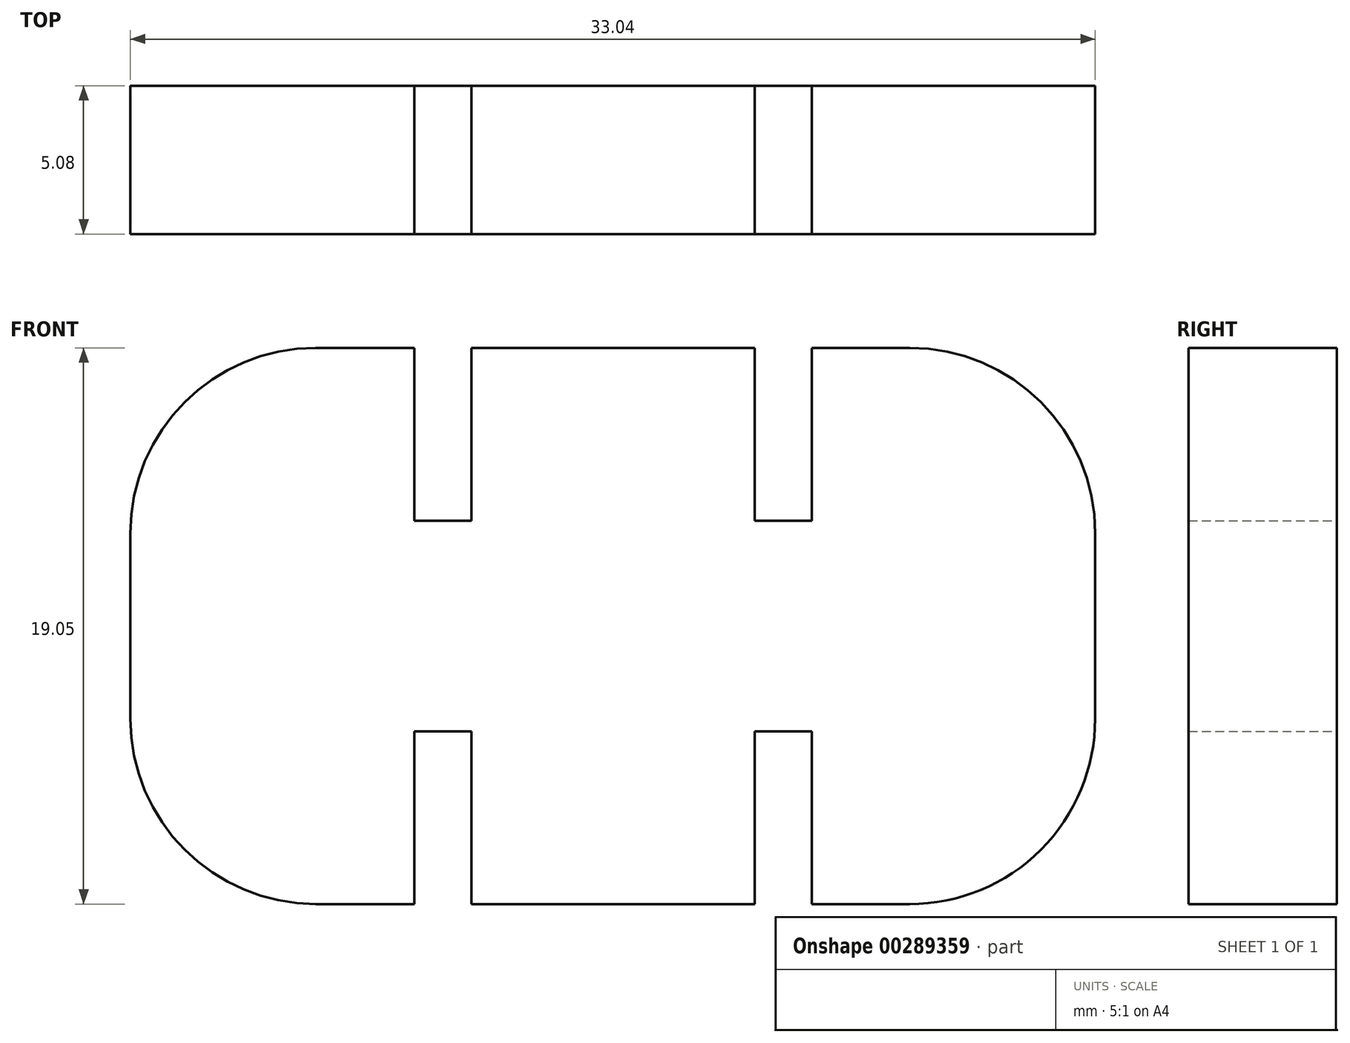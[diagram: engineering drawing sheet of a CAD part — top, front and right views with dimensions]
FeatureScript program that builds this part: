
annotation { "Feature Type Name" : "Feature", "Feature Type Description" : "" }
export const myFeature = defineFeature(function(context is Context, id is Id, definition is map)
    precondition{}
    {
        {
            var Q0;
            Q0=qCreatedBy(makeId("Front.planeOp"),FACE);
            var sketch = newSketch(context, id + "F0", { "sketchPlane" : qUnion([Q0])});
            skLineSegment(sketch, "E0", {"start": v(-67.37, 34.52) * mm, "end": v(-67.37, 28.17) * mm});
            skLineSegment(sketch, "E1", {"start": v(-61.02, 40.87) * mm, "end": v(-57.65, 40.87) * mm});
            skLineSegment(sketch, "E2", {"start": v(-57.65, 40.87) * mm, "end": v(-57.65, 34.95) * mm});
            skLineSegment(sketch, "E3", {"start": v(-57.65, 34.95) * mm, "end": v(-55.7, 34.95) * mm});
            skLineSegment(sketch, "E4", {"start": v(-55.7, 34.95) * mm, "end": v(-55.7, 40.87) * mm});
            skLineSegment(sketch, "E5", {"start": v(-55.7, 40.87) * mm, "end": v(-45.99, 40.87) * mm});
            skLineSegment(sketch, "E6", {"start": v(-45.99, 40.87) * mm, "end": v(-45.99, 34.95) * mm});
            skLineSegment(sketch, "E7", {"start": v(-45.99, 34.95) * mm, "end": v(-44.03, 34.95) * mm});
            skLineSegment(sketch, "E8", {"start": v(-44.03, 34.95) * mm, "end": v(-44.03, 40.87) * mm});
            skLineSegment(sketch, "E9", {"start": v(-44.03, 40.87) * mm, "end": v(-40.68, 40.87) * mm});
            skLineSegment(sketch, "E10", {"start": v(-34.33, 34.52) * mm, "end": v(-34.33, 28.17) * mm});
            skLineSegment(sketch, "E11", {"start": v(-61.02, 21.82) * mm, "end": v(-57.65, 21.82) * mm});
            skLineSegment(sketch, "E12", {"start": v(-57.65, 21.82) * mm, "end": v(-57.65, 27.74) * mm});
            skLineSegment(sketch, "E13", {"start": v(-57.65, 27.74) * mm, "end": v(-55.7, 27.74) * mm});
            skLineSegment(sketch, "E14", {"start": v(-55.7, 27.74) * mm, "end": v(-55.7, 21.82) * mm});
            skLineSegment(sketch, "E15", {"start": v(-55.7, 21.82) * mm, "end": v(-45.99, 21.82) * mm});
            skLineSegment(sketch, "E16", {"start": v(-45.99, 21.82) * mm, "end": v(-45.99, 27.74) * mm});
            skLineSegment(sketch, "E17", {"start": v(-45.99, 27.74) * mm, "end": v(-44.03, 27.74) * mm});
            skLineSegment(sketch, "E18", {"start": v(-44.03, 27.74) * mm, "end": v(-44.03, 21.82) * mm});
            skLineSegment(sketch, "E19", {"start": v(-44.03, 21.82) * mm, "end": v(-40.68, 21.82) * mm});
            skPoint(sketch, "E20.visualSharp", {"position": v(-67.37, 40.87) * mm});
            skArc(sketch, "E20.filletArc", {"start": v(-61.02, 40.87) * mm, "mid": v(-65.51, 39.01) * mm, "end": v(-67.37, 34.52) * mm});
            skPoint(sketch, "E21.visualSharp", {"position": v(-34.33, 40.87) * mm});
            skArc(sketch, "E21.filletArc", {"start": v(-34.33, 34.52) * mm, "mid": v(-36.19, 39) * mm, "end": v(-40.68, 40.87) * mm});
            skPoint(sketch, "E22.visualSharp", {"position": v(-34.33, 21.82) * mm});
            skArc(sketch, "E22.filletArc", {"start": v(-40.68, 21.82) * mm, "mid": v(-36.19, 23.68) * mm, "end": v(-34.33, 28.17) * mm});
            skPoint(sketch, "E23.visualSharp", {"position": v(-67.37, 21.82) * mm});
            skArc(sketch, "E23.filletArc", {"start": v(-67.37, 28.17) * mm, "mid": v(-65.51, 23.68) * mm, "end": v(-61.02, 21.82) * mm});
            skSolve(sketch);
        }
        {
            var Q0;
            Q0=makeQuery(id+"F0.imprint","IMPRINT",FACE,{"disambiguationData":[TD([[makeQuery(id+"F0.imprint","IMPRINT",EDGE,{"derivedFrom":sQuery(id+"F0.wireOp",EDGE,"E0")}),1.0]])]});
            extrude(context, id + "F1", {"entities" : qUnion([Q0]), "depth" : 5.08 * mm});
        }
    });
